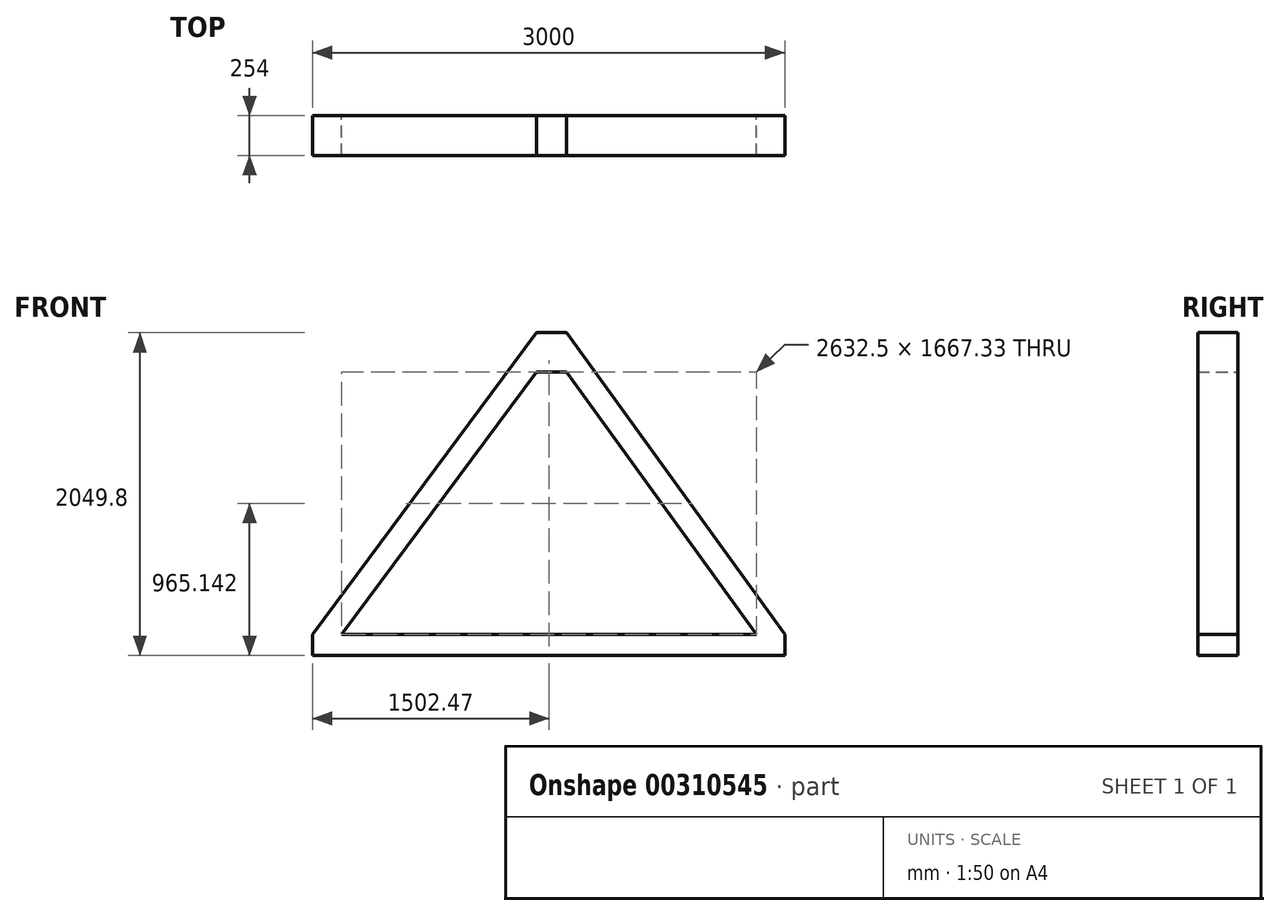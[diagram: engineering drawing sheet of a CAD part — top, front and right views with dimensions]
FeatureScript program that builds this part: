
annotation { "Feature Type Name" : "Feature", "Feature Type Description" : "" }
export const myFeature = defineFeature(function(context is Context, id is Id, definition is map)
    precondition{}
    {
        {
            var Q0;
            Q0=qCreatedBy(makeId("Front.planeOp"),FACE);
            var sketch = newSketch(context, id + "F0", { "sketchPlane" : qUnion([Q0])});
            skLineSegment(sketch, "E0.bottom", {"start": v(-1518.9, -1090.64) * mm, "end": v(1481.1, -1090.64) * mm});
            skLineSegment(sketch, "E0.top", {"start": v(-1518.9, -959.16) * mm, "end": v(1481.1, -959.16) * mm});
            skLineSegment(sketch, "E0.left", {"start": v(-1518.9, -1090.64) * mm, "end": v(-1518.9, -959.16) * mm});
            skLineSegment(sketch, "E0.right", {"start": v(1481.1, -1090.64) * mm, "end": v(1481.1, -959.16) * mm});
            skLineSegment(sketch, "E1.bottom", {"start": v(95.62, -959.16) * mm, "end": v(-95.62, -959.16) * mm});
            skLineSegment(sketch, "E1.top", {"start": v(95.62, 959.16) * mm, "end": v(-95.62, 959.16) * mm});
            skLineSegment(sketch, "E1.left", {"start": v(95.62, -959.16) * mm, "end": v(95.62, 959.16) * mm});
            skLineSegment(sketch, "E1.right", {"start": v(-95.62, -959.16) * mm, "end": v(-95.62, 959.16) * mm});
            skPoint(sketch, "E1.middle", {"position": v(0, 0) * mm});
            skLineSegment(sketch, "E2", {"start": v(-95.62, 959.16) * mm, "end": v(-1518.9, -959.16) * mm});
            skLineSegment(sketch, "E3", {"start": v(-95.62, 708.17) * mm, "end": v(-1332.67, -959.16) * mm});
            skLineSegment(sketch, "E4", {"start": v(95.62, 959.16) * mm, "end": v(1481.1, -959.16) * mm});
            skLineSegment(sketch, "E5", {"start": v(-95.62, 708.17) * mm, "end": v(95.62, 708.17) * mm});
            skLineSegment(sketch, "E6", {"start": v(95.62, 708.17) * mm, "end": v(1299.83, -959.16) * mm});
            skCircle(sketch, "E7", {"center": v(0, 0) * mm, "radius": 50.8 * mm});
            skSolve(sketch);
        }
        {
            var Q0;
            {var subQ1=sQuery(id+"F0.wireOp",EDGE,"E1.bottom");Q0=makeQuery(id+"F0.imprint","IMPRINT",FACE,{"disambiguationData":[TD([[makeQuery(id+"F0.imprint","IMPRINT",EDGE,{"derivedFrom":subQ1}),-1.0]])]});}
            var Q1;
            {var subQ0=sQuery(id+"F0.wireOp",EDGE,"E4");Q1=makeQuery(id+"F0.imprint","IMPRINT",FACE,{"disambiguationData":[TD([[makeQuery(id+"F0.imprint","IMPRINT",EDGE,{"derivedFrom":subQ0}),-1.0]])]});}
            var Q2;
            {var subQ0=sQuery(id+"F0.wireOp",EDGE,"E1.top");Q2=makeQuery(id+"F0.imprint","IMPRINT",FACE,{"disambiguationData":[TD([[makeQuery(id+"F0.imprint","IMPRINT",EDGE,{"derivedFrom":subQ0}),1.0]])]});}
            var Q3;
            {var subQ0=sQuery(id+"F0.wireOp",EDGE,"E2");Q3=makeQuery(id+"F0.imprint","IMPRINT",FACE,{"disambiguationData":[TD([[makeQuery(id+"F0.imprint","IMPRINT",EDGE,{"derivedFrom":subQ0}),1.0]])]});}
            var Q4;
            Q4=makeQuery(id+"F0.imprint","IMPRINT",FACE,{"disambiguationData":[TD([[makeQuery(id+"F0.imprint","IMPRINT",EDGE,{"derivedFrom":sQuery(id+"F0.wireOp",EDGE,"E0.bottom")}),1.0]])]});
            extrude(context, id + "F1", {"entities" : qUnion([Q0, Q1, Q2, Q3, Q4]), "depth" : 254 * mm});
        }
    });
